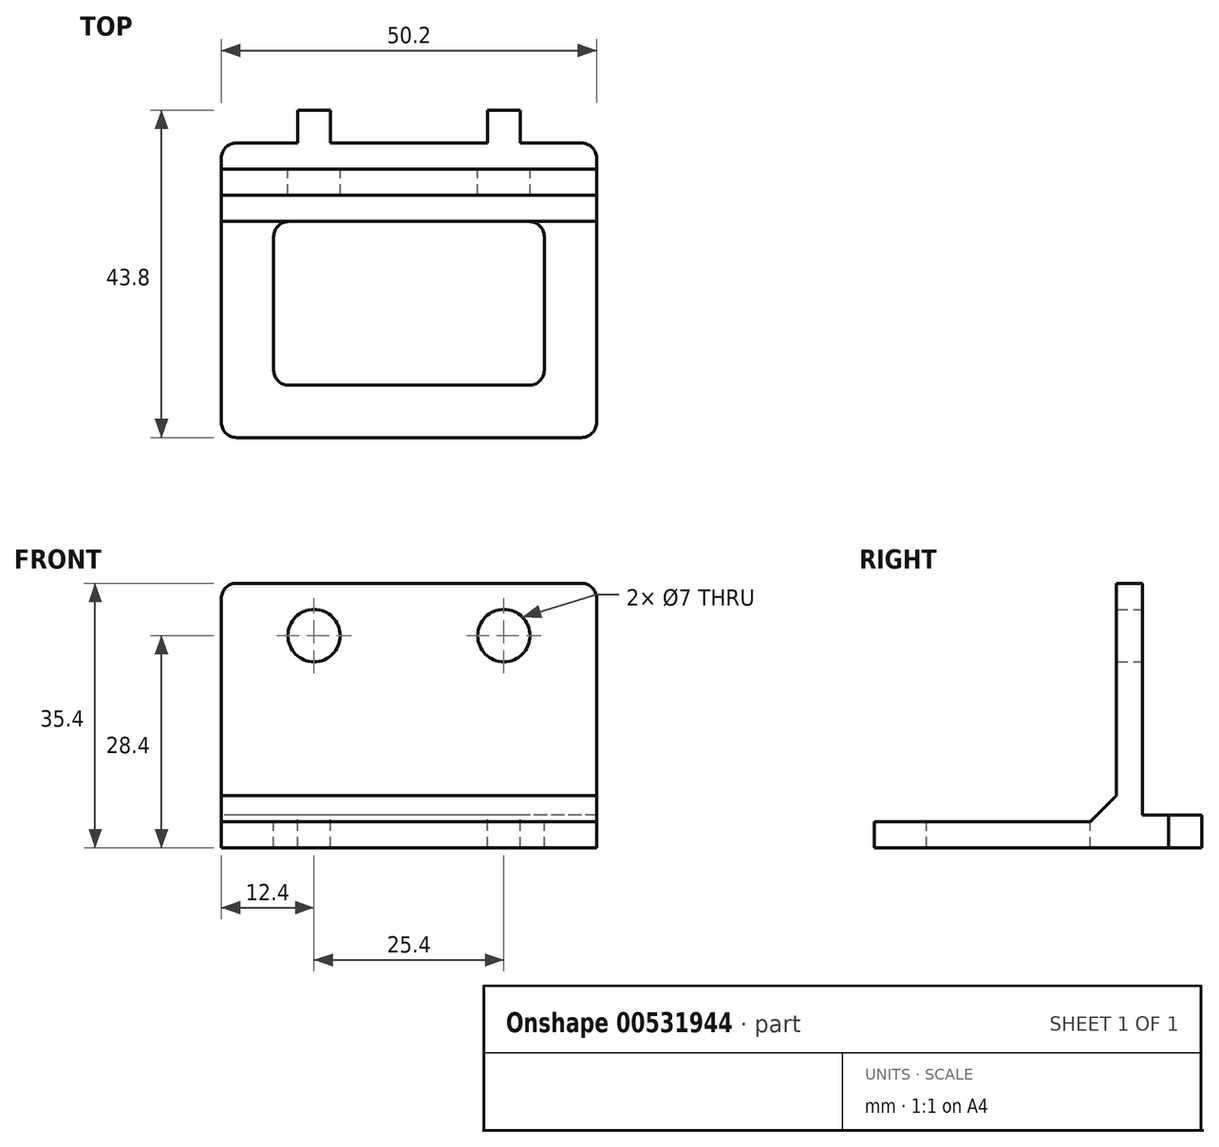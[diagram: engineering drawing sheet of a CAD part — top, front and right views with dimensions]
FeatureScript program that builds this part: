
annotation { "Feature Type Name" : "Feature", "Feature Type Description" : "" }
export const myFeature = defineFeature(function(context is Context, id is Id, definition is map)
    precondition{}
    {
        {
            var Q0;
            Q0=qCreatedBy(makeId("Top.planeOp"),FACE);
            var sketch = newSketch(context, id + "F0", { "sketchPlane" : qUnion([Q0])});
            skLineSegment(sketch, "E0.bottom", {"start": v(-16.2, 16.2) * mm, "end": v(16.2, 16.2) * mm});
            skLineSegment(sketch, "E0.top", {"start": v(-16.2, -16.2) * mm, "end": v(16.2, -16.2) * mm});
            skLineSegment(sketch, "E0.left", {"start": v(-16.2, 16.2) * mm, "end": v(-16.2, -16.2) * mm});
            skLineSegment(sketch, "E0.right", {"start": v(16.2, 16.2) * mm, "end": v(16.2, -16.2) * mm});
            skPoint(sketch, "E0.middle", {"position": v(0, 0) * mm});
            skSolve(sketch);
        }
        {
            var Q0;
            Q0=makeQuery(id+"F0.imprint","IMPRINT",FACE,{"disambiguationData":[TD([[makeQuery(id+"F0.imprint","IMPRINT",EDGE,{"derivedFrom":sQuery(id+"F0.wireOp",EDGE,"E0.bottom")}),-1.0]])]});
            extrude(context, id + "F1", {"entities" : qUnion([Q0]), "depth" : 25.4 * mm, "offsetDistance" : 25 * mm});
        }
        {
            var Q0;
            Q0=makeQuery(id+"F1.opExtrude","CAP_FACE",FACE,{"disambiguationData":[OSD([sQuery(id+"F0.wireOp",EDGE,"E0.bottom"),sQuery(id+"F0.wireOp",EDGE,"E0.top"),sQuery(id+"F0.wireOp",EDGE,"E0.left"),sQuery(id+"F0.wireOp",EDGE,"E0.right")])],"isStart":false});
            var sketch = newSketch(context, id + "F2", { "sketchPlane" : qUnion([Q0])});
            skLineSegment(sketch, "E1", {"start": v(-16.2, -16.2) * mm, "end": v(-16.2, -10.86) * mm});
            skLineSegment(sketch, "E2", {"start": v(16.2, 16.2) * mm, "end": v(16.2, 12.7) * mm});
            skLineSegment(sketch, "E3.bottom", {"start": v(16.2, 12.7) * mm, "end": v(-16.2, 12.7) * mm});
            skLineSegment(sketch, "E3.top", {"start": v(16.2, 16.2) * mm, "end": v(-16.2, 16.2) * mm});
            skLineSegment(sketch, "E3.left", {"start": v(16.2, 12.7) * mm, "end": v(16.2, 16.2) * mm});
            skLineSegment(sketch, "E3.right", {"start": v(-16.2, 12.7) * mm, "end": v(-16.2, 16.2) * mm});
            skSolve(sketch);
        }
        {
            var Q0;
            {var subQ0=sQuery(id+"F2.wireOp",EDGE,"E1");Q0=makeQuery(id+"F2.imprint","IMPRINT",FACE,{"disambiguationData":[TD([[makeQuery(id+"F2.imprint","IMPRINT",EDGE,{"derivedFrom":subQ0}),1.0]])]});}
            extrude(context, id + "F3", {"entities" : qUnion([Q0]), "operationType" : NewBodyOperationType.REMOVE, "oppositeDirection" : true, "depth" : 21.9 * mm, "offsetDistance" : 25 * mm});
        }
        {
            var Q0;
            Q0=makeQuery(id+"F3.boolean.opBoolean","COPY",FACE,{"derivedFrom":makeQuery(id+"F3.opExtrude","CAP_FACE",FACE,{"disambiguationData":[OSD([sQuery(id+"F0.wireOp",EDGE,"E0.top"),sQuery(id+"F0.wireOp",EDGE,"E0.left"),sQuery(id+"F0.wireOp",EDGE,"E0.right"),sQuery(id+"F2.wireOp",EDGE,"E1"),sQuery(id+"F2.wireOp",EDGE,"E3.bottom")])],"isStart":false})});
            var sketch = newSketch(context, id + "F4", { "sketchPlane" : qUnion([Q0])});
            skLineSegment(sketch, "E4", {"start": v(-16.2, -16.2) * mm, "end": v(-12.7, -16.2) * mm});
            skLineSegment(sketch, "E5", {"start": v(-12.7, -16.2) * mm, "end": v(-12.7, -12.7) * mm});
            skLineSegment(sketch, "E6", {"start": v(16.2, 12.7) * mm, "end": v(12.7, 12.7) * mm});
            skLineSegment(sketch, "E7", {"start": v(12.7, 12.7) * mm, "end": v(12.7, 9.2) * mm});
            skLineSegment(sketch, "E8.bottom", {"start": v(-12.7, -12.7) * mm, "end": v(12.7, -12.7) * mm});
            skLineSegment(sketch, "E8.top", {"start": v(-12.7, 9.2) * mm, "end": v(12.7, 9.2) * mm});
            skLineSegment(sketch, "E8.left", {"start": v(-12.7, -12.7) * mm, "end": v(-12.7, 9.2) * mm});
            skLineSegment(sketch, "E8.right", {"start": v(12.7, -12.7) * mm, "end": v(12.7, 9.2) * mm});
            skSolve(sketch);
        }
        {
            var Q0;
            Q0=makeQuery(id+"F4.imprint","IMPRINT",FACE,{"disambiguationData":[TD([[makeQuery(id+"F4.imprint","IMPRINT",EDGE,{"derivedFrom":sQuery(id+"F4.wireOp",EDGE,"E8.bottom")}),1.0]])]});
            extrude(context, id + "F5", {"entities" : qUnion([Q0]), "operationType" : NewBodyOperationType.REMOVE, "endBound" : BoundingType.THROUGH_ALL, "oppositeDirection" : true, "depth" : 25 * mm, "offsetDistance" : 25 * mm});
        }
        {
            var Q0;
            Q0=makeQuery(id+"F1.opExtrude","SWEPT_FACE",FACE,{"disambiguationData":[OSD([sQuery(id+"F0.wireOp",EDGE,"E0.left")])]});
            var sketch = newSketch(context, id + "F6", { "sketchPlane" : qUnion([Q0])});
            skLineSegment(sketch, "E9", {"start": v(-12.7, 3.5) * mm, "end": v(-9.2, 3.5) * mm});
            skLineSegment(sketch, "E10", {"start": v(-12.7, 3.5) * mm, "end": v(-12.7, 7) * mm});
            skLineSegment(sketch, "E11", {"start": v(-9.2, 3.5) * mm, "end": v(-12.7, 7) * mm});
            skSolve(sketch);
        }
        {
            var Q0;
            Q0=makeQuery(id+"F6.imprint","IMPRINT",FACE,{"disambiguationData":[TD([[makeQuery(id+"F6.imprint","IMPRINT",EDGE,{"derivedFrom":sQuery(id+"F6.wireOp",EDGE,"E9")}),1.0]])]});
            var Q1;
            Q1=makeQuery(id+"F1.opExtrude","SWEPT_FACE",FACE,{"disambiguationData":[OSD([sQuery(id+"F0.wireOp",EDGE,"E0.right")])]});
            extrude(context, id + "F7", {"entities" : qUnion([Q0]), "operationType" : NewBodyOperationType.ADD, "endBound" : BoundingType.UP_TO_SURFACE, "oppositeDirection" : true, "depth" : 25 * mm, "endBoundEntityFace" : qUnion([Q1]), "offsetDistance" : 25 * mm});
        }
        {
            var Q0;
            {var subQ0=sQuery(id+"F0.wireOp",EDGE,"E0.right");Q0=makeQuery(id+"F7.boolean.opBoolean","MERGE",FACE,{"derivedFrom":[makeQuery(id+"F1.opExtrude","SWEPT_FACE",FACE,{"disambiguationData":[OSD([subQ0])]}),makeQuery(id+"F7.opExtrude","CAP_FACE",FACE,{"disambiguationData":[OSD([subQ0])],"isStart":false})]});}
            extrude(context, id + "F8", {"entities" : qUnion([Q0]), "operationType" : NewBodyOperationType.ADD, "depth" : 3.5 * mm, "offsetDistance" : 25 * mm});
        }
        {
            var Q0;
            Q0=makeQuery(id+"F7.boolean.opBoolean","MERGE",FACE,{"derivedFrom":[makeQuery(id+"F1.opExtrude","SWEPT_FACE",FACE,{"disambiguationData":[OSD([sQuery(id+"F0.wireOp",EDGE,"E0.left")])]}),makeQuery(id+"F7.opExtrude","CAP_FACE",FACE,{"disambiguationData":[OSD([sQuery(id+"F6.wireOp",EDGE,"E9"),sQuery(id+"F6.wireOp",EDGE,"E10"),sQuery(id+"F6.wireOp",EDGE,"E11")])],"isStart":true})]});
            extrude(context, id + "F9", {"entities" : qUnion([Q0]), "operationType" : NewBodyOperationType.ADD, "depth" : 3.5 * mm, "offsetDistance" : 25 * mm});
        }
        {
            var Q0;
            {var subQ0=sQuery(id+"F0.wireOp",EDGE,"E0.top");Q0=makeQuery(id+"F9.boolean.opBoolean","MERGE",FACE,{"derivedFrom":[makeQuery(id+"F8.boolean.opBoolean","MERGE",FACE,{"derivedFrom":[makeQuery(id+"F1.opExtrude","SWEPT_FACE",FACE,{"disambiguationData":[OSD([subQ0])]}),makeQuery(id+"F8.opExtrude","SWEPT_FACE",FACE,{"disambiguationData":[OSD([subQ0,sQuery(id+"F0.wireOp",EDGE,"E0.right")])]})]}),makeQuery(id+"F9.opExtrude","SWEPT_FACE",FACE,{"disambiguationData":[OSD([subQ0,sQuery(id+"F0.wireOp",EDGE,"E0.left")])]})]});}
            extrude(context, id + "F10", {"entities" : qUnion([Q0]), "operationType" : NewBodyOperationType.ADD, "depth" : 3.5 * mm, "offsetDistance" : 25 * mm});
        }
        {
            var Q0;
            {var subQ0=sQuery(id+"F0.wireOp",EDGE,"E0.bottom");Q0=makeQuery(id+"F9.boolean.opBoolean","MERGE",FACE,{"derivedFrom":[makeQuery(id+"F8.boolean.opBoolean","MERGE",FACE,{"derivedFrom":[makeQuery(id+"F1.opExtrude","SWEPT_FACE",FACE,{"disambiguationData":[OSD([subQ0])]}),makeQuery(id+"F8.opExtrude","SWEPT_FACE",FACE,{"disambiguationData":[OSD([subQ0,sQuery(id+"F0.wireOp",EDGE,"E0.right")])]})]}),makeQuery(id+"F9.opExtrude","SWEPT_FACE",FACE,{"disambiguationData":[OSD([subQ0,sQuery(id+"F0.wireOp",EDGE,"E0.left")])]})]});}
            var sketch = newSketch(context, id + "F11", { "sketchPlane" : qUnion([Q0])});
            skPoint(sketch, "E12", {"position": v(-19.7, 3.5) * mm});
            skLineSegment(sketch, "E13.bottom", {"start": v(-19.7, 3.5) * mm, "end": v(19.7, 3.5) * mm});
            skLineSegment(sketch, "E13.top", {"start": v(-19.7, 0) * mm, "end": v(19.7, 0) * mm});
            skLineSegment(sketch, "E13.left", {"start": v(-19.7, 3.5) * mm, "end": v(-19.7, 0) * mm});
            skLineSegment(sketch, "E13.right", {"start": v(19.7, 3.5) * mm, "end": v(19.7, 0) * mm});
            skSolve(sketch);
        }
        {
            var Q0;
            Q0=makeQuery(id+"F11.imprint","IMPRINT",FACE,{"disambiguationData":[TD([[makeQuery(id+"F11.imprint","IMPRINT",EDGE,{"derivedFrom":sQuery(id+"F11.wireOp",EDGE,"E13.bottom")}),-1.0]])]});
            extrude(context, id + "F12", {"entities" : qUnion([Q0]), "operationType" : NewBodyOperationType.ADD, "depth" : 3.5 * mm, "offsetDistance" : 25 * mm});
        }
        {
            var Q0;
            {var subQ0=sQuery(id+"F0.wireOp",EDGE,"E0.left");var subQ1=sQuery(id+"F0.wireOp",EDGE,"E0.right");Q0=makeQuery(id+"F9.boolean.opBoolean","MERGE",FACE,{"derivedFrom":[makeQuery(id+"F8.boolean.opBoolean","MERGE",FACE,{"derivedFrom":[makeQuery(id+"F1.opExtrude","CAP_FACE",FACE,{"disambiguationData":[OSD([sQuery(id+"F0.wireOp",EDGE,"E0.bottom"),sQuery(id+"F0.wireOp",EDGE,"E0.top"),subQ0,subQ1])],"isStart":false}),makeQuery(id+"F8.opExtrude","SWEPT_FACE",FACE,{"disambiguationData":[OSD([subQ1]),TDD([makeQuery(id+"F1.opExtrude","CAP_EDGE",EDGE,{"disambiguationData":[OSD([subQ1])],"isStart":false})])]})]}),makeQuery(id+"F9.opExtrude","SWEPT_FACE",FACE,{"disambiguationData":[OSD([subQ0]),TDD([makeQuery(id+"F1.opExtrude","CAP_EDGE",EDGE,{"disambiguationData":[OSD([subQ0])],"isStart":false})])]})]});}
            extrude(context, id + "F13", {"entities" : qUnion([Q0]), "operationType" : NewBodyOperationType.ADD, "depth" : 10 * mm, "offsetDistance" : 25 * mm});
        }
        {
            var Q0;
            {var subQ0=sQuery(id+"F0.wireOp",EDGE,"E0.right");var subQ1=sQuery(id+"F0.wireOp",EDGE,"E0.left");var subQ2=sQuery(id+"F0.wireOp",EDGE,"E0.bottom");Q0=makeQuery(id+"F13.boolean.opBoolean","MERGE",FACE,{"derivedFrom":[makeQuery(id+"F9.boolean.opBoolean","MERGE",FACE,{"derivedFrom":[makeQuery(id+"F8.boolean.opBoolean","MERGE",FACE,{"derivedFrom":[makeQuery(id+"F1.opExtrude","SWEPT_FACE",FACE,{"disambiguationData":[OSD([subQ2])]}),makeQuery(id+"F8.opExtrude","SWEPT_FACE",FACE,{"disambiguationData":[OSD([subQ2,subQ0])]})]}),makeQuery(id+"F9.opExtrude","SWEPT_FACE",FACE,{"disambiguationData":[OSD([subQ2,subQ1])]})]}),makeQuery(id+"F13.opExtrude","SWEPT_FACE",FACE,{"disambiguationData":[OSD([subQ2,subQ1,subQ0])]})]});}
            var sketch = newSketch(context, id + "F14", { "sketchPlane" : qUnion([Q0])});
            skPoint(sketch, "E14", {"position": v(-12.7, 28.4) * mm});
            skPoint(sketch, "E15", {"position": v(12.7, 28.4) * mm});
            skSolve(sketch);
        }
        {
            var Q0;
            Q0=sQuery(id+"F14.wireOp",VERTEX,"E14");
            var Q1;
            Q1=sQuery(id+"F14.wireOp",VERTEX,"E15");
            var Q2;
            Q2=makeQuery(id+"F1.opExtrude","SWEPT_BODY",BODY,{"disambiguationData":[OSD([sQuery(id+"F0.wireOp",EDGE,"E0.bottom"),sQuery(id+"F0.wireOp",EDGE,"E0.top"),sQuery(id+"F0.wireOp",EDGE,"E0.left"),sQuery(id+"F0.wireOp",EDGE,"E0.right")])]});
            hole(context, id + "F15", {"style" : HoleStyle.SIMPLE, "endStyle" : HoleEndStyle.THROUGH, "holeDiameter" : 7 * mm, "isTappedThrough" : true, "tappedDepth" : 1 * mm, "tapClearance" : 3, "locations" : qUnion([Q0, Q1]), "scope" : qUnion([Q2])});
        }
        {
            var Q0;
            Q0=makeQuery(id+"F9piRCkLwfh8P6E_1.boolean.opBoolean","MERGE",FACE,{"derivedFrom":[makeQuery(id+"F12.opExtrude","SWEPT_FACE",FACE,{"disambiguationData":[OSD([sQuery(id+"F11.wireOp",EDGE,"E13.bottom")])]}),makeQuery(id+"F9piRCkLwfh8P6E_1.opExtrude","SWEPT_FACE",FACE,{"disambiguationData":[OSD([sQuery(id+"FYIe6LbPkeTgSfv_1.wireOp",EDGE,"IJTBLjRN-jrmw-mfig-qvl3-cg5BqmVv3ECp.top")])]}),makeQuery(id+"F9piRCkLwfh8P6E_1.opExtrude","SWEPT_FACE",FACE,{"disambiguationData":[OSD([sQuery(id+"FYIe6LbPkeTgSfv_1.wireOp",EDGE,"yrXcAWqd-ghLK-hsOL-5WNR-7RsMBuYfyUqk.top")])]})]});
            extrude(context, id + "F16", {"entities" : qUnion([Q0]), "operationType" : NewBodyOperationType.ADD, "depth" : 0.9 * mm, "offsetDistance" : 25 * mm});
        }
        {
            var Q0;
            {var subQ0=sQuery(id+"F11.wireOp",EDGE,"E13.bottom");Q0=makeQuery(id+"F16.boolean.opBoolean","MERGE",FACE,{"derivedFrom":[makeQuery(id+"F12.opExtrude","CAP_FACE",FACE,{"disambiguationData":[OSD([subQ0,sQuery(id+"F11.wireOp",EDGE,"E13.top"),sQuery(id+"F11.wireOp",EDGE,"E13.left"),sQuery(id+"F11.wireOp",EDGE,"E13.right")])],"isStart":false}),makeQuery(id+"F16.opExtrude","SWEPT_FACE",FACE,{"disambiguationData":[OSD([subQ0]),TDD([makeQuery(id+"F12.opExtrude","CAP_EDGE",EDGE,{"disambiguationData":[OSD([subQ0])],"isStart":false})])]})]});}
            var sketch = newSketch(context, id + "F17", { "sketchPlane" : qUnion([Q0])});
            skPoint(sketch, "E16", {"position": v(-10.5, 4.4) * mm});
            skPoint(sketch, "E17", {"position": v(-14.9, 0) * mm});
            skLineSegment(sketch, "E18.bottom", {"start": v(-14.9, 0) * mm, "end": v(-10.5, 0) * mm});
            skLineSegment(sketch, "E18.top", {"start": v(-14.9, 4.4) * mm, "end": v(-10.5, 4.4) * mm});
            skLineSegment(sketch, "E18.left", {"start": v(-14.9, 0) * mm, "end": v(-14.9, 4.4) * mm});
            skLineSegment(sketch, "E18.right", {"start": v(-10.5, 0) * mm, "end": v(-10.5, 4.4) * mm});
            skPoint(sketch, "E19", {"position": v(10.5, 4.4) * mm});
            skPoint(sketch, "E20", {"position": v(14.9, 0) * mm});
            skLineSegment(sketch, "E21.bottom", {"start": v(14.9, 0) * mm, "end": v(10.5, 0) * mm});
            skLineSegment(sketch, "E21.top", {"start": v(14.9, 4.4) * mm, "end": v(10.5, 4.4) * mm});
            skLineSegment(sketch, "E21.left", {"start": v(14.9, 0) * mm, "end": v(14.9, 4.4) * mm});
            skLineSegment(sketch, "E21.right", {"start": v(10.5, 0) * mm, "end": v(10.5, 4.4) * mm});
            skSolve(sketch);
        }
        {
            var Q0;
            Q0=makeQuery(id+"F17.imprint","IMPRINT",FACE,{"disambiguationData":[TD([[makeQuery(id+"F17.imprint","IMPRINT",EDGE,{"derivedFrom":sQuery(id+"F17.wireOp",EDGE,"E18.bottom")}),-1.0]])]});
            var Q1;
            Q1=makeQuery(id+"F17.imprint","IMPRINT",FACE,{"disambiguationData":[TD([[makeQuery(id+"F17.imprint","IMPRINT",EDGE,{"derivedFrom":sQuery(id+"F17.wireOp",EDGE,"E21.bottom")}),-1.0]])]});
            extrude(context, id + "F18", {"entities" : qUnion([Q0, Q1]), "operationType" : NewBodyOperationType.ADD, "depth" : 4.4 * mm, "offsetDistance" : 25 * mm});
        }
        {
            var Q0;
            {var subQ0=sQuery(id+"F11.wireOp",EDGE,"E13.left");var subQ1=sQuery(id+"F0.wireOp",EDGE,"E0.right");Q0=makeQuery(id+"F16.boolean.opBoolean","MERGE",FACE,{"derivedFrom":[makeQuery(id+"F13.boolean.opBoolean","MERGE",FACE,{"derivedFrom":[makeQuery(id+"F12.boolean.opBoolean","MERGE",FACE,{"derivedFrom":[makeQuery(id+"F10.boolean.opBoolean","MERGE",FACE,{"derivedFrom":[makeQuery(id+"F8.opExtrude","CAP_FACE",FACE,{"disambiguationData":[OSD([subQ1])],"isStart":false}),makeQuery(id+"F10.opExtrude","SWEPT_FACE",FACE,{"disambiguationData":[OSD([sQuery(id+"F0.wireOp",EDGE,"E0.top"),subQ1])]})]}),makeQuery(id+"F12.opExtrude","SWEPT_FACE",FACE,{"disambiguationData":[OSD([subQ0])]})]}),makeQuery(id+"F13.opExtrude","SWEPT_FACE",FACE,{"disambiguationData":[OSD([subQ1])]})]}),makeQuery(id+"F16.opExtrude","SWEPT_FACE",FACE,{"disambiguationData":[OSD([sQuery(id+"F0.wireOp",EDGE,"E0.bottom"),subQ1,sQuery(id+"F11.wireOp",EDGE,"E13.bottom"),subQ0])]})]});}
            extrude(context, id + "F19", {"entities" : qUnion([Q0]), "operationType" : NewBodyOperationType.ADD, "depth" : 5.4 * mm, "offsetDistance" : 25 * mm});
        }
        {
            var Q0;
            {var subQ0=sQuery(id+"F11.wireOp",EDGE,"E13.right");var subQ1=sQuery(id+"F0.wireOp",EDGE,"E0.left");Q0=makeQuery(id+"F16.boolean.opBoolean","MERGE",FACE,{"derivedFrom":[makeQuery(id+"F13.boolean.opBoolean","MERGE",FACE,{"derivedFrom":[makeQuery(id+"F12.boolean.opBoolean","MERGE",FACE,{"derivedFrom":[makeQuery(id+"F10.boolean.opBoolean","MERGE",FACE,{"derivedFrom":[makeQuery(id+"F9.opExtrude","CAP_FACE",FACE,{"disambiguationData":[OSD([subQ1,sQuery(id+"F6.wireOp",EDGE,"E9"),sQuery(id+"F6.wireOp",EDGE,"E10"),sQuery(id+"F6.wireOp",EDGE,"E11")])],"isStart":false}),makeQuery(id+"F10.opExtrude","SWEPT_FACE",FACE,{"disambiguationData":[OSD([sQuery(id+"F0.wireOp",EDGE,"E0.top"),subQ1])]})]}),makeQuery(id+"F12.opExtrude","SWEPT_FACE",FACE,{"disambiguationData":[OSD([subQ0])]})]}),makeQuery(id+"F13.opExtrude","SWEPT_FACE",FACE,{"disambiguationData":[OSD([subQ1])]})]}),makeQuery(id+"F16.opExtrude","SWEPT_FACE",FACE,{"disambiguationData":[OSD([sQuery(id+"F0.wireOp",EDGE,"E0.bottom"),subQ1,sQuery(id+"F11.wireOp",EDGE,"E13.bottom"),subQ0])]})]});}
            extrude(context, id + "F20", {"entities" : qUnion([Q0]), "operationType" : NewBodyOperationType.ADD, "depth" : 5.4 * mm, "offsetDistance" : 25 * mm});
        }
        {
            var Q0;
            Q0=makeQuery(id+"F5.boolean.opBoolean","COPY",FACE,{"derivedFrom":makeQuery(id+"F5.opExtrude","SWEPT_FACE",FACE,{"disambiguationData":[OSD([sQuery(id+"F4.wireOp",EDGE,"E8.left")])]})});
            extrude(context, id + "F21", {"entities" : qUnion([Q0]), "operationType" : NewBodyOperationType.REMOVE, "oppositeDirection" : true, "depth" : 5.4 * mm, "offsetDistance" : 25 * mm});
        }
        {
            var Q0;
            Q0=makeQuery(id+"F5.boolean.opBoolean","COPY",FACE,{"derivedFrom":makeQuery(id+"F5.opExtrude","SWEPT_FACE",FACE,{"disambiguationData":[OSD([sQuery(id+"F4.wireOp",EDGE,"E8.right")])]})});
            extrude(context, id + "F22", {"entities" : qUnion([Q0]), "operationType" : NewBodyOperationType.REMOVE, "oppositeDirection" : true, "depth" : 5.4 * mm, "offsetDistance" : 25 * mm});
        }
        {
            var Q0;
            Q0=makeQuery(id+"F20.opExtrude","CAP_EDGE",EDGE,{"disambiguationData":[OSD([sQuery(id+"F0.wireOp",EDGE,"E0.left")])],"isStart":false});
            var Q1;
            {var subQ0=sQuery(id+"F11.wireOp",EDGE,"E13.right");var subQ1=sQuery(id+"F11.wireOp",EDGE,"E13.bottom");var subQ2=sQuery(id+"F0.wireOp",EDGE,"E0.left");var subQ3=sQuery(id+"F0.wireOp",EDGE,"E0.bottom");Q1=makeQuery(id+"F20.opExtrude","CAP_EDGE",EDGE,{"disambiguationData":[OSD([subQ3,subQ2,subQ1,subQ0]),TDD([makeQuery(id+"F16.boolean.opBoolean","MERGE",EDGE,{"derivedFrom":[makeQuery(id+"F12.opExtrude","CAP_EDGE",EDGE,{"disambiguationData":[OSD([subQ0])],"isStart":false}),makeQuery(id+"F16.opExtrude","SWEPT_EDGE",EDGE,{"disambiguationData":[OSD([subQ3,subQ2,subQ1,subQ0]),TDD([makeQuery(id+"F12.opExtrude","CAP_VERTEX",VERTEX,{"disambiguationData":[OSD([subQ3,subQ2,subQ1,subQ0])],"isStart":false})])]})]})])],"isStart":false});}
            var Q2;
            Q2=makeQuery(id+"F20.opExtrude","CAP_EDGE",EDGE,{"disambiguationData":[OSD([sQuery(id+"F0.wireOp",EDGE,"E0.top"),sQuery(id+"F0.wireOp",EDGE,"E0.left")])],"isStart":false});
            var Q3;
            {var subQ0=sQuery(id+"F0.wireOp",EDGE,"E0.right");var subQ1=sQuery(id+"F0.wireOp",EDGE,"E0.top");Q3=makeQuery(id+"F19.opExtrude","CAP_EDGE",EDGE,{"disambiguationData":[OSD([subQ1,subQ0]),TDD([makeQuery(id+"F10.opExtrude","CAP_EDGE",EDGE,{"disambiguationData":[OSD([subQ1,subQ0])],"isStart":false})])],"isStart":false});}
            var Q4;
            Q4=makeQuery(id+"F22.boolean.opBoolean","COPY",EDGE,{"derivedFrom":makeQuery(id+"F22.opExtrude","CAP_EDGE",EDGE,{"disambiguationData":[OSD([sQuery(id+"F4.wireOp",EDGE,"E7"),sQuery(id+"F4.wireOp",EDGE,"E8.top"),sQuery(id+"F4.wireOp",EDGE,"E8.right")])],"isStart":false})});
            var Q5;
            Q5=makeQuery(id+"F22.boolean.opBoolean","COPY",EDGE,{"derivedFrom":makeQuery(id+"F22.opExtrude","CAP_EDGE",EDGE,{"disambiguationData":[OSD([sQuery(id+"F4.wireOp",EDGE,"E8.bottom"),sQuery(id+"F4.wireOp",EDGE,"E8.right")])],"isStart":false})});
            var Q6;
            Q6=makeQuery(id+"F21.boolean.opBoolean","COPY",EDGE,{"derivedFrom":makeQuery(id+"F21.opExtrude","CAP_EDGE",EDGE,{"disambiguationData":[OSD([sQuery(id+"F4.wireOp",EDGE,"E8.top"),sQuery(id+"F4.wireOp",EDGE,"E8.left")])],"isStart":false})});
            var Q7;
            Q7=makeQuery(id+"F21.boolean.opBoolean","COPY",EDGE,{"derivedFrom":makeQuery(id+"F21.opExtrude","CAP_EDGE",EDGE,{"disambiguationData":[OSD([sQuery(id+"F4.wireOp",EDGE,"E5"),sQuery(id+"F4.wireOp",EDGE,"E8.bottom"),sQuery(id+"F4.wireOp",EDGE,"E8.left")])],"isStart":false})});
            var Q8;
            {var subQ0=sQuery(id+"F11.wireOp",EDGE,"E13.left");var subQ1=sQuery(id+"F11.wireOp",EDGE,"E13.bottom");var subQ2=sQuery(id+"F0.wireOp",EDGE,"E0.right");var subQ3=sQuery(id+"F0.wireOp",EDGE,"E0.bottom");Q8=makeQuery(id+"F19.opExtrude","CAP_EDGE",EDGE,{"disambiguationData":[OSD([subQ3,subQ2,subQ1,subQ0]),TDD([makeQuery(id+"F16.boolean.opBoolean","MERGE",EDGE,{"derivedFrom":[makeQuery(id+"F12.opExtrude","CAP_EDGE",EDGE,{"disambiguationData":[OSD([subQ0])],"isStart":false}),makeQuery(id+"F16.opExtrude","SWEPT_EDGE",EDGE,{"disambiguationData":[OSD([subQ3,subQ2,subQ1,subQ0]),TDD([makeQuery(id+"F12.opExtrude","CAP_VERTEX",VERTEX,{"disambiguationData":[OSD([subQ3,subQ2,subQ1,subQ0])],"isStart":false})])]})]})])],"isStart":false});}
            var Q9;
            Q9=makeQuery(id+"F19.opExtrude","CAP_EDGE",EDGE,{"disambiguationData":[OSD([sQuery(id+"F0.wireOp",EDGE,"E0.right")])],"isStart":false});
            fillet(context, id + "F23", {"entities" : qUnion([Q0, Q1, Q2, Q3, Q4, Q5, Q6, Q7, Q8, Q9]), "radius" : 2 * mm, "tangentPropagation" : true, "allowEdgeOverflow" : false});
        }
    });
